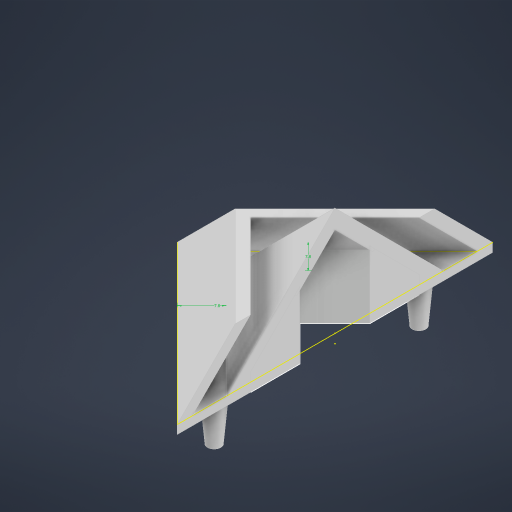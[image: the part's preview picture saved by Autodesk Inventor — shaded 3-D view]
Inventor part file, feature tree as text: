
AUTODESK INVENTOR PART (.ipt)
format: ipt  version: 2023 (Build 270158000, 158)  size: 403,456 bytes
history: native  units: mm
features: extrude x16, sketch x15, plane x6, split x2, shell x2, draft x1
ambient origin geometry x8: Origin, YZ Plane, XZ Plane, XY Plane, X Axis, Y Axis, Z Axis, Center Point
bodies: Solid1 (feature_tree), Solid4 (feature_tree)
feature tree (42):
  extrude  "Extrusion1"  Depth=2.0mm TaperAngle=0.0deg
  sketch  "Sketch3"  dims[d1=50.0mm d2=2.0mm d3=0.0mm]
  sketch  "Sketch12"  dims[d41=70.71mm d42=50.0mm d43=50.0mm]
  plane  "Work Plane5"
  plane  "Work Plane6"
  extrude  "Extrusion10"  Depth=50.0mm
  split  "Split3"
  shell  "Shell3"  Thickness=50.0mm
  sketch  "Sketch13"  dims[d44=10.0mm d45=0.0mm d46=0.0mm d47=7.8mm]
  plane  "Work Plane9"
  plane  "Work Plane10"
  extrude  "Extrusion18"  TaperAngle=0.0deg  [1 undecoded]
  split  "Split5"
  shell  "Shell5"  Thickness=7.8mm
  extrude  "Extrusion24"  Depth=2.0mm
  extrude  "Extrusion25"  Depth=7.8mm
  extrude  "Extrusion26"  Depth=2.0mm
  extrude  "Extrusion27"  Depth=2.0mm TaperAngle=0.0deg
  draft  "FaceDraft3"
  plane  "Work Plane12"
  extrude  "Extrusion28"  Depth=10.0mm
  sketch  "Sketch31"  dims[d117=3.0mm d118=3.0mm]
  extrude  "Extrusion29"  Depth=3.0mm
  extrude  "Extrusion30"  Depth=10.0mm
  sketch  "Sketch33"  dims[d119=10.0mm d120=0.0mm d121=0.872665mm]
  sketch  "Sketch34"  dims[d122=-15.0mm d123=30.0mm d124=0.0mm]
  extrude  "Extrusion31"  Depth=30.0mm TaperAngle=0.0deg
  extrude  "Extrusion32"  Depth=10.0mm TaperAngle=0.0deg
  extrude  "Extrusion33"  Depth=10.0mm
  extrude  "Extrusion34"  Depth=2.45mm TaperAngle=0.0deg
  extrude  "Extrusion35"  Depth=2.45mm TaperAngle=0.0deg
  extrude  "Extrusion36"  Depth=2.45mm TaperAngle=0.0deg
  sketch  "Sketch25"  dims[d48=7.8mm d49=2.0mm]
  sketch  "Sketch27"  dims[d52=7.8mm d53=7.8mm]
  sketch  "Sketch28"  dims[d85=10.0mm d86=0.0mm d87=2.0mm]
  sketch  "Sketch29"  dims[d110=2.0mm d111=0.0mm d112=2.0mm d113=0.0mm]
  plane  "Work Plane11"
  sketch  "Sketch30"  dims[d114=10.0mm d115=0.0mm d116=3.0mm]
  sketch  "Sketch35"  dims[d125=10.0mm d126=0.0mm d127=10.0mm d128=0.0mm]
  sketch  "Sketch37"  dims[d129=10.0mm d130=10.0mm]
  sketch  "Sketch38"  dims[d131=2.45mm d132=0.0mm d133=2.45mm d134=0.0mm]
  sketch  "Sketch39"  dims[d135=2.45mm d136=0.0mm d138=2.45mm d139=0.0mm d140=2.45mm d141=0.0mm d142=2.45mm d143=0.0mm d88=0.872665mm d137=0.5mm]
note: 1 required parameter value undecoded (feature->parameter linkage not recoverable at this tier; creation-order binding heuristic only, values carry confidence <= 0.55)
